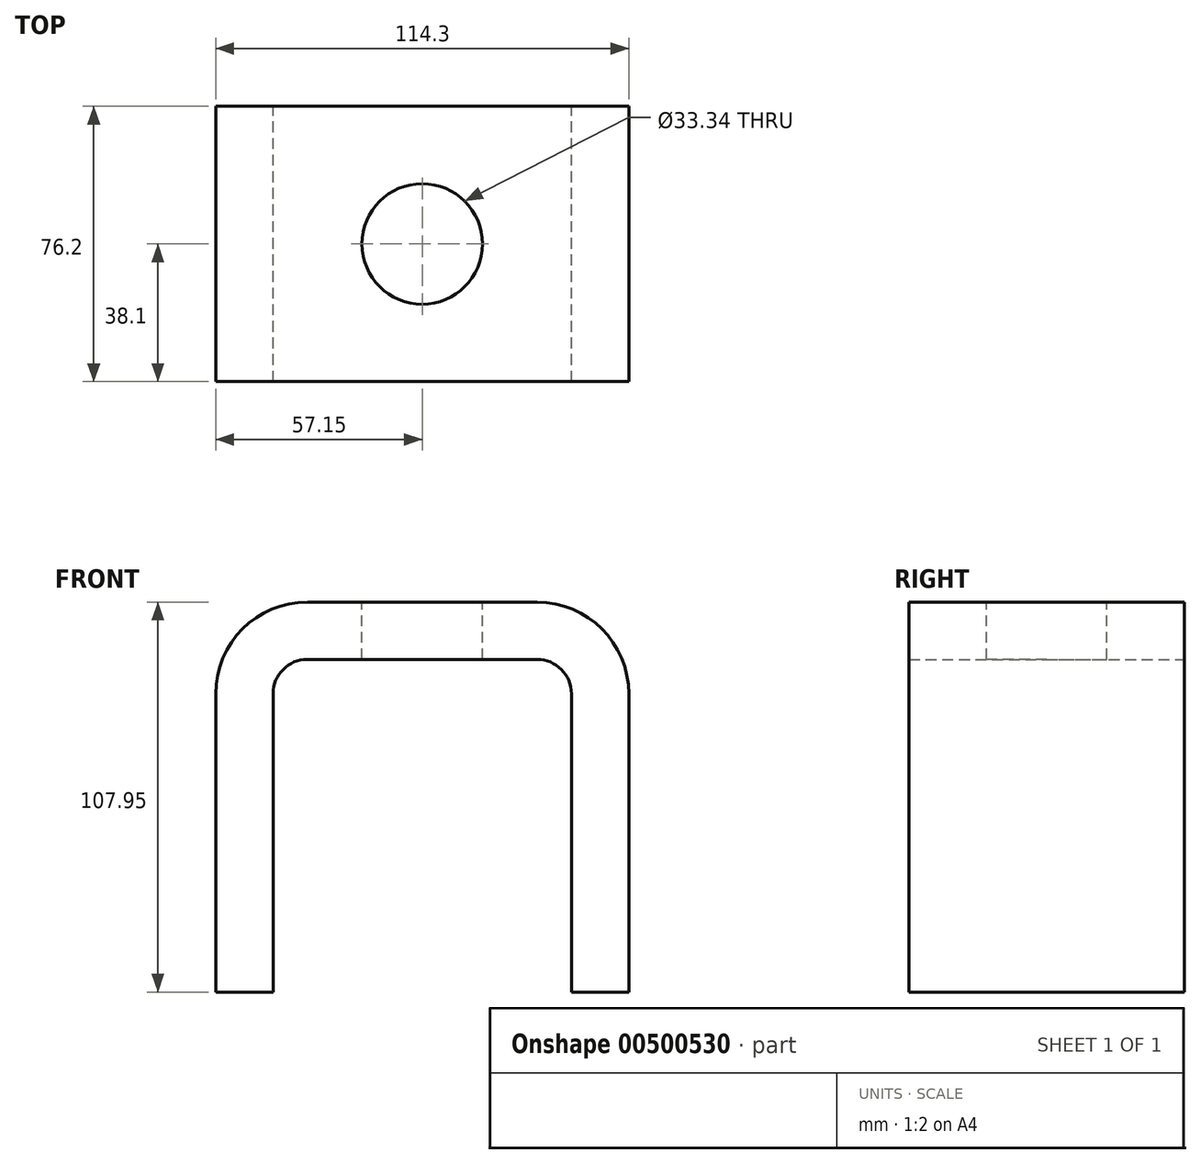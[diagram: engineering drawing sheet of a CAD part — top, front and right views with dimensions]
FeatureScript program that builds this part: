
annotation { "Feature Type Name" : "Feature", "Feature Type Description" : "" }
export const myFeature = defineFeature(function(context is Context, id is Id, definition is map)
    precondition{}
    {
        {
            var Q0;
            Q0=qCreatedBy(makeId("Front.planeOp"),FACE);
            var sketch = newSketch(context, id + "F0", { "sketchPlane" : qUnion([Q0])});
            skLineSegment(sketch, "E0.top", {"start": v(41.28, 46.04) * mm, "end": v(-41.28, 46.04) * mm});
            skLineSegment(sketch, "E0.left", {"start": v(41.28, -46.04) * mm, "end": v(41.28, 46.04) * mm});
            skLineSegment(sketch, "E0.right", {"start": v(-41.28, -46.04) * mm, "end": v(-41.28, 46.04) * mm});
            skPoint(sketch, "E0.middle", {"position": v(0, 0) * mm});
            skLineSegment(sketch, "E1.0", {"start": v(57.15, -46.04) * mm, "end": v(57.15, 46.04) * mm});
            skLineSegment(sketch, "E2.0", {"start": v(41.28, 61.91) * mm, "end": v(-41.28, 61.91) * mm});
            skLineSegment(sketch, "E3.0", {"start": v(-57.15, -46.04) * mm, "end": v(-57.15, 46.04) * mm});
            skLineSegment(sketch, "E4", {"start": v(-57.15, 46.04) * mm, "end": v(-57.15, 61.91) * mm});
            skLineSegment(sketch, "E5", {"start": v(-57.15, 61.91) * mm, "end": v(-41.28, 61.91) * mm});
            skLineSegment(sketch, "E6", {"start": v(41.28, 61.91) * mm, "end": v(57.15, 61.91) * mm});
            skLineSegment(sketch, "E7", {"start": v(57.15, 61.91) * mm, "end": v(57.15, 46.04) * mm});
            skLineSegment(sketch, "E8", {"start": v(57.15, -46.04) * mm, "end": v(41.28, -46.04) * mm});
            skLineSegment(sketch, "E9", {"start": v(-41.28, -46.04) * mm, "end": v(-57.15, -46.04) * mm});
            skSolve(sketch);
        }
        {
            var Q0;
            Q0 = qSketchRegion(id + "F0", true);
            extrude(context, id + "F1", {"entities" : qUnion([Q0]), "endBound" : BoundingType.SYMMETRIC, "depth" : 76.2 * mm});
        }
        {
            var Q0;
            Q0=makeQuery(id+"F1.opExtrude","SWEPT_EDGE",EDGE,{"disambiguationData":[OSD([sQuery(id+"F0.wireOp",EDGE,"E0.top"),sQuery(id+"F0.wireOp",EDGE,"E0.right")])]});
            var Q1;
            Q1=makeQuery(id+"F1.opExtrude","SWEPT_EDGE",EDGE,{"disambiguationData":[OSD([sQuery(id+"F0.wireOp",EDGE,"E0.top"),sQuery(id+"F0.wireOp",EDGE,"E0.left")])]});
            fillet(context, id + "F2", {"entities" : qUnion([Q0, Q1]), "radius" : 9.52 * mm, "tangentPropagation" : true, "allowEdgeOverflow" : false});
        }
        {
            var Q0;
            Q0=makeQuery(id+"F1.opExtrude","SWEPT_EDGE",EDGE,{"disambiguationData":[OSD([sQuery(id+"F0.wireOp",EDGE,"E4"),sQuery(id+"F0.wireOp",EDGE,"E5")])]});
            var Q1;
            Q1=makeQuery(id+"F1.opExtrude","SWEPT_EDGE",EDGE,{"disambiguationData":[OSD([sQuery(id+"F0.wireOp",EDGE,"E6"),sQuery(id+"F0.wireOp",EDGE,"E7")])]});
            fillet(context, id + "F3", {"entities" : qUnion([Q0, Q1]), "radius" : 25.4 * mm, "tangentPropagation" : true, "allowEdgeOverflow" : false});
        }
        {
            var Q0;
            Q0=makeQuery(id+"F1.opExtrude","SWEPT_FACE",FACE,{"disambiguationData":[OSD([sQuery(id+"F0.wireOp",EDGE,"E2.0"),sQuery(id+"F0.wireOp",EDGE,"E5"),sQuery(id+"F0.wireOp",EDGE,"E6")])]});
            var sketch = newSketch(context, id + "F4", { "sketchPlane" : qUnion([Q0])});
            skCircle(sketch, "E10", {"center": v(0, 0) * mm, "radius": 16.67 * mm});
            skSolve(sketch);
        }
        {
            var Q0;
            Q0 = qSketchRegion(id + "F4", true);
            extrude(context, id + "F5", {"entities" : qUnion([Q0]), "operationType" : NewBodyOperationType.REMOVE, "oppositeDirection" : true, "depth" : 25.4 * mm});
        }
    });
